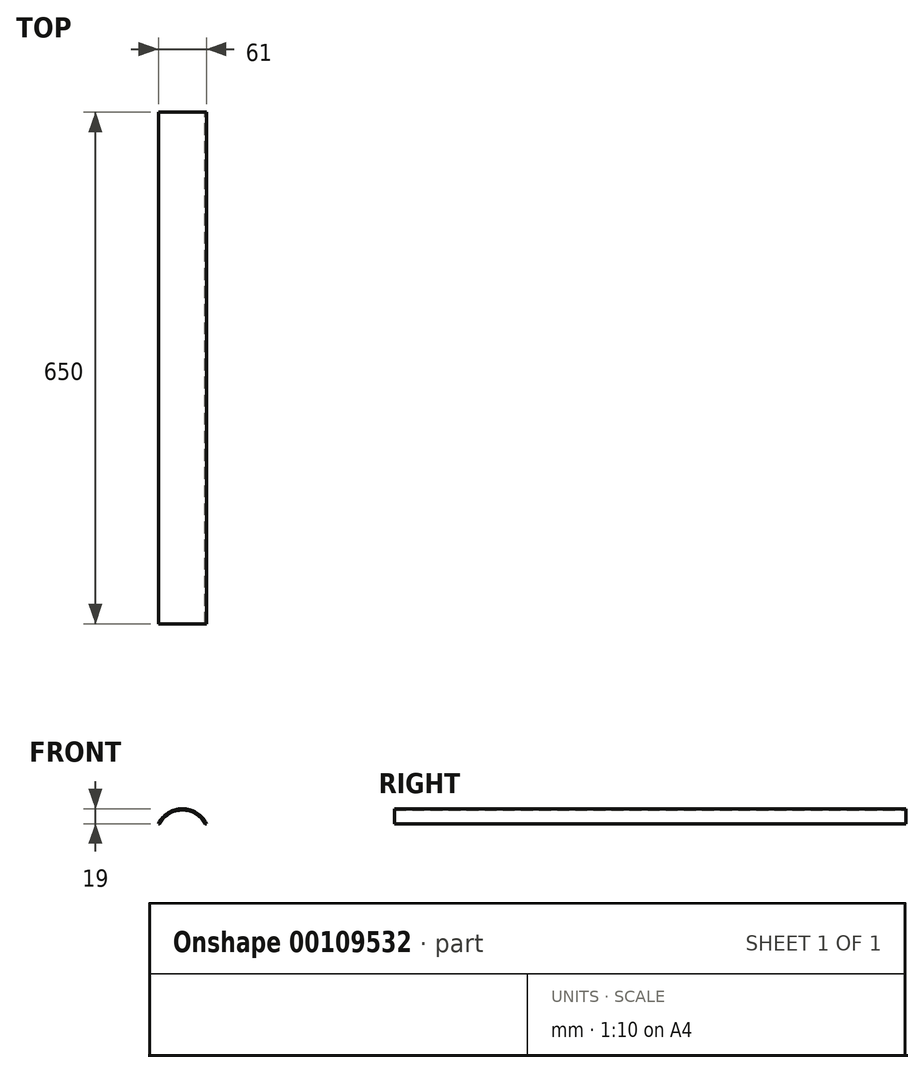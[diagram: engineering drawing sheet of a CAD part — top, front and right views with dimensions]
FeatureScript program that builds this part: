
annotation { "Feature Type Name" : "Feature", "Feature Type Description" : "" }
export const myFeature = defineFeature(function(context is Context, id is Id, definition is map)
    precondition{}
    {
        {
            var Q0;
            Q0=qCreatedBy(makeId("Front.planeOp"),FACE);
            var sketch = newSketch(context, id + "F0", { "sketchPlane" : qUnion([Q0])});
            skLineSegment(sketch, "E0", {"start": v(-30.5, 8.78) * mm, "end": v(30.5, 8.78) * mm, "construction": true});
            skLineSegment(sketch, "E1", {"start": v(0, 8.78) * mm, "end": v(0, 27.78) * mm, "construction": true});
            skPoint(sketch, "E1.endSnap0", {"position": v(0, 8.78) * mm});
            skArc(sketch, "E2", {"start": v(30.5, 8.78) * mm, "mid": v(0, 27.78) * mm, "end": v(-30.5, 8.78) * mm});
            skArc(sketch, "E3.0", {"start": v(28.82, 8.78) * mm, "mid": v(0, 26.28) * mm, "end": v(-28.82, 8.78) * mm});
            skLineSegment(sketch, "E4", {"start": v(-30.5, 8.78) * mm, "end": v(-28.82, 8.78) * mm});
            skLineSegment(sketch, "E5", {"start": v(30.5, 8.78) * mm, "end": v(28.82, 8.78) * mm});
            skSolve(sketch);
        }
        {
            var Q0;
            Q0=qSketchRegion(id+"F0",true);
            extrude(context, id + "F1", {"entities" : qUnion([Q0]), "depth" : 650 * mm});
        }
    });
